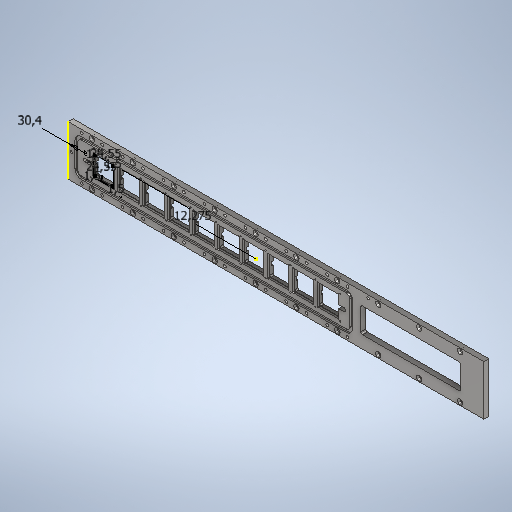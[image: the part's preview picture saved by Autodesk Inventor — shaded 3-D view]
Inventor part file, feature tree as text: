
AUTODESK INVENTOR PART (.ipt)
format: ipt  version: 2025.2 (Build 292293000, 293)  size: 838,144 bytes
history: native  units: mm
features: sketch x14, extrude x8, hole x6, pattern_linear x5, fillet x1
ambient origin geometry x8: Origin, YZ Plane, XZ Plane, XY Plane, X Axis, Y Axis, Z Axis, Center Point
bodies: Volumenkörper1 (feature_tree)
feature tree (34):
  extrude  "Extrusion1"  Depth=500.0mm
  extrude  "Extrusion3"  Depth=30.0mm
  pattern_linear  "Rechteckige Anordnung2"  Count1=10  [1 undecoded]
  extrude  "Extrusion6"  Depth=2.0mm
  extrude  "Extrusion7"  Depth=7.0mm
  hole  "Bohrung12"  [1 undecoded]
  extrude  "Extrusion9"  Depth=3.55mm
  hole  "Bohrung15"  [1 undecoded]
  hole  "Bohrung16"  [1 undecoded]
  pattern_linear  "Rechteckige Anordnung7"  Spacing1=6.5mm  [1 undecoded]
  extrude  "Extrusion10"  Depth=6.5mm
  pattern_linear  "Rechteckige Anordnung8"  Spacing1=4.0mm  [1 undecoded]
  extrude  "Extrusion11"  Depth=2.0mm
  hole  "Festschraubung Zentrierplatte"  [1 undecoded]
  pattern_linear  "Rechteckige Anordnung9"  Spacing1=0.0mm  [1 undecoded]
  hole  "Durchgangsbohrung"  [1 undecoded]
  pattern_linear  "Durchgangsbohrungen"  Spacing1=4.0mm  [1 undecoded]
  extrude  "Extrusion12"  Depth=4.0mm
  fillet  "Rundung1"  Radius=3.0mm
  hole  "Bohrung21"  [1 undecoded]
  sketch  "Skizze1"  dims[d0=274.0mm d1=500.0mm]
  sketch  "Skizze4"  dims[d2=60.0mm d3=30.0mm]
  sketch  "Skizze18"  dims[d4=6.0mm d5=0.0mm]
  sketch  "Skizze19"  dims[d29=30.4mm]
  sketch  "Skizze21"  dims[d35=24.55mm]
  sketch  "Skizze26"  dims[d36=24.55mm]
  sketch  "Skizze27"  dims[d40=0.0mm d41=0.0mm d42=100.0mm d44=30.0mm]
  sketch  "Skizze28"  dims[d154=2.0mm d155=2.0mm]
  sketch  "Skizze33"  dims[d157=0.0mm d158=0.0mm d159=7.0mm]
  sketch  "Skizze34"  dims[d160=2.0mm d166=4.0mm]
  sketch  "Skizze36"  dims[d167=4.0mm d168=3.55mm]
  sketch  "Skizze37"  dims[d169=1.9mm d170=0.0mm d180=30.0mm]
  sketch  "Skizze38"  dims[d181=3.75mm]
  sketch  "Skizze39"  dims[d182=3.0mm d183=6.0mm d184=4.0mm d185=2.0mm d186=90.0deg d187=8.0mm d188=20.594885mm d242=6.5mm d243=6.5mm d244=6.5mm d246=4.0mm d247=2.0mm d248=10.5mm d249=0.0mm d250=0.0mm d252=8.1mm d253=4.0mm d254=4.0mm d255=3.0mm d256=2.0mm d257=1.567mm d258=4.0mm d259=3.023mm d260=2.0mm d261=14.3117mm d262=6.3mm d263=20.594885mm d264=3.0mm d265=2.0mm d266=1.567mm d267=4.0mm d268=4.0mm d269=2.0mm d270=90.0deg d271=5.692mm d272=20.594885mm d273=110.0mm d275=30.0mm d298=12.275mm d299=1.5mm d300=1.5mm d301=1.5mm d302=1.5mm d304=0.75mm d305=0.55mm d306=0.55mm d307=0.55mm d308=0.75mm d309=0.55mm d310=0.75mm d311=0.75mm d312=2.2mm d313=0.0mm d314=100.0mm d316=30.0mm d317=2.0mm d318=2.0mm d319=2.2mm d320=0.0mm d322=28.6mm d323=3.75mm d324=3.4mm d325=6.0mm d326=6.5mm d327=3.0mm d328=90.0deg d329=4.2mm d330=20.594885mm d331=100.0mm d333=49.2mm d334=20.0mm d336=52.5mm d337=3.75mm d338=3.4mm d339=0.5mm d340=4.0mm d341=2.0mm d342=90.0deg d343=0.875mm d344=20.594885mm d345=16.3mm d346=140.0mm d348=24.6mm d349=20.0mm d351=52.5mm d352=15.0mm d353=15.0mm d354=28.0mm d355=120.0mm d356=0.0mm d357=0.0mm d358=2.0mm d359=360.7mm d360=3.0mm d361=6.0mm d362=4.0mm d363=2.0mm d364=90.0deg d365=8.0mm d366=20.594885mm d367=3.75mm d13=0.0mm d14=0.0mm d15=0.0mm d16=0.0mm d87=1.0mm d88=1.0mm d89=1.0mm d90=0.15mm d91=0.25mm d92=0.375mm d93=14.3117mm d94=0.75mm d95=20.594885mm d96=0.0625mm d97=0.75mm d98=0.375mm d139=1.0mm d140=1.0mm d141=1.0mm d142=0.15mm d143=0.25mm d144=0.375mm d145=14.3117mm d146=0.75mm d147=20.594885mm d148=0.0625mm d149=0.75mm d150=0.375mm d368=0.0625mm d369=0.75mm d370=0.375mm]
note: 11 required parameter values undecoded (feature->parameter linkage not recoverable at this tier; creation-order binding heuristic only, values carry confidence <= 0.55)
